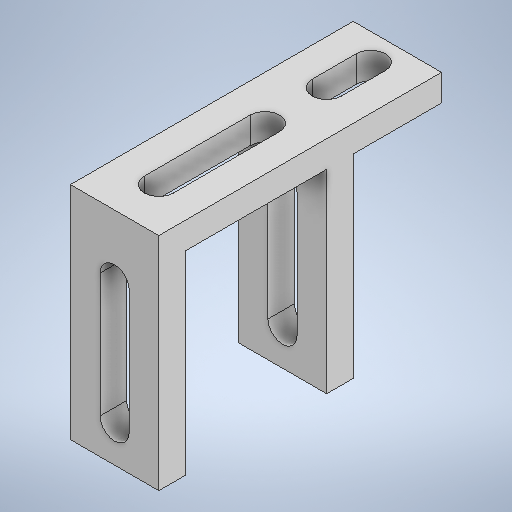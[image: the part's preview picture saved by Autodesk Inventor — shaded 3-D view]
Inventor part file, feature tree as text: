
AUTODESK INVENTOR PART (.ipt)
format: ipt  version: 2025.2 (Build 292293000, 293)  size: 267,264 bytes
history: native  units: mm
features: extrude x3, sketch x3
ambient origin geometry x8: Origin, YZ Plane, XZ Plane, XY Plane, X Axis, Y Axis, Z Axis, Center Point
bodies: Solid1 (feature_tree)
feature tree (6):
  extrude  "Extrusion1"  Depth=22.0mm
  extrude  "Extrusion2"  Depth=16.0mm
  extrude  "Extrusion3"  Depth=10.0mm
  sketch  "Sketch1"  dims[d0=25.0mm d1=22.0mm]
  sketch  "Sketch2"  dims[d2=19.0mm d3=16.0mm]
  sketch  "Sketch3"  dims[d4=3.0mm d5=10.0mm d6=10.0mm d7=0.0mm d8=2.0mm d9=2.0mm d10=3.3mm d11=2.0mm d12=3.0mm d13=3.3mm d14=0.0mm d15=0.0mm d16=4.0mm d17=4.0mm d18=3.3mm d19=0.0mm d20=0.0mm]
